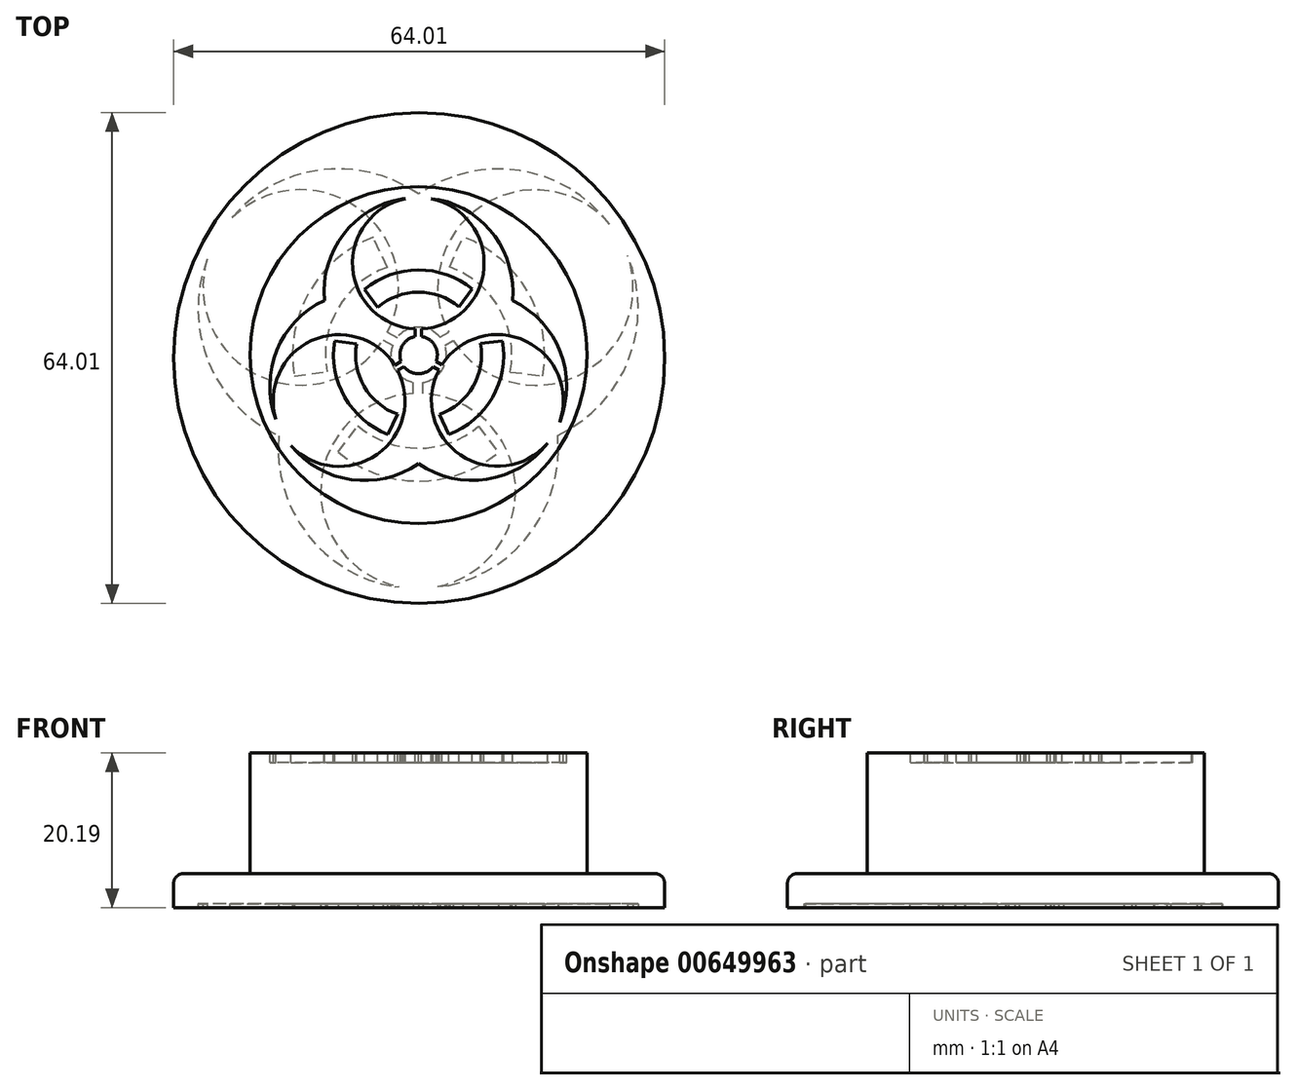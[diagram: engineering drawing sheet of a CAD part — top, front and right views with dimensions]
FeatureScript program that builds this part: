
annotation { "Feature Type Name" : "Feature", "Feature Type Description" : "" }
export const myFeature = defineFeature(function(context is Context, id is Id, definition is map)
    precondition{}
    {
        {
            var Q0;
            Q0=qCreatedBy(makeId("Top.planeOp"),FACE);
            var sketch = newSketch(context, id + "F0", { "sketchPlane" : qUnion([Q0])});
            skCircle(sketch, "E0", {"center": v(0.07, -0.4) * mm, "radius": 32 * mm});
            skSolve(sketch);
        }
        {
            var Q0;
            Q0=makeQuery(id+"F0.imprint","IMPRINT",FACE,{"disambiguationData":[TD([[makeQuery(id+"F0.imprint","IMPRINT",EDGE,{"derivedFrom":sQuery(id+"F0.wireOp",EDGE,"E0")}),1.0]])]});
            extrude(context, id + "F1", {"entities" : qUnion([Q0]), "depth" : 4.44 * mm, "offsetDistance" : 25.4 * mm});
        }
        {
            var Q0;
            Q0=makeQuery(id+"F1.opExtrude","CAP_FACE",FACE,{"disambiguationData":[OSD([sQuery(id+"F0.wireOp",EDGE,"E0")])],"isStart":false});
            var sketch = newSketch(context, id + "F2", { "sketchPlane" : qUnion([Q0])});
            skCircle(sketch, "E1", {"center": v(0, 0) * mm, "radius": 21.97 * mm});
            skSolve(sketch);
        }
        {
            var Q0;
            Q0 = qSketchRegion(id + "F2", true);
            extrude(context, id + "F3", {"entities" : qUnion([Q0]), "operationType" : NewBodyOperationType.ADD, "depth" : 15.75 * mm, "offsetDistance" : 25.4 * mm});
        }
        {
            var Q0;
            Q0=makeQuery(id+"F1.opExtrude","CAP_EDGE",EDGE,{"disambiguationData":[OSD([sQuery(id+"F0.wireOp",EDGE,"E0")])],"isStart":false});
            fillet(context, id + "F4", {"entities" : qUnion([Q0]), "radius" : 1.27 * mm, "tangentPropagation" : true, "allowEdgeOverflow" : false});
        }
        {
            var Q0;
            Q0=makeQuery(id+"F3.opExtrude","CAP_FACE",FACE,{"disambiguationData":[OSD([sQuery(id+"F2.wireOp",EDGE,"E1")])],"isStart":false});
            var sketch = newSketch(context, id + "F5", { "sketchPlane" : qUnion([Q0])});
            skArc(sketch, "E2", {"start": v(-0.47, 2.4) * mm, "mid": v(-2.13, 1.2) * mm, "end": v(-2.29, -0.86) * mm});
            skArc(sketch, "E3", {"start": v(2.64, -1.99) * mm, "mid": v(5.47, -13.06) * mm, "end": v(16.8, -11.51) * mm});
            skPoint(sketch, "E3.first.point", {"position": v(1.98, -8.2) * mm});
            skPoint(sketch, "E3.second.point", {"position": v(5.37, 1.13) * mm});
            skPoint(sketch, "E3.third.point", {"position": v(18.4, -3.15) * mm});
            skArc(sketch, "E4", {"start": v(-3.12, -1.32) * mm, "mid": v(-13.95, 1.86) * mm, "end": v(-18.6, -8.42) * mm});
            skPoint(sketch, "E4.first.point", {"position": v(-17.7, -1.47) * mm});
            skPoint(sketch, "E4.second.point", {"position": v(-6.4, 1.68) * mm});
            skPoint(sketch, "E4.third.point", {"position": v(-5.15, -12.78) * mm});
            skArc(sketch, "E5", {"start": v(0.4, 3.4) * mm, "mid": v(8.5, 11.33) * mm, "end": v(1.65, 20.36) * mm});
            skPoint(sketch, "E5.first.point", {"position": v(-6.26, 17.86) * mm});
            skPoint(sketch, "E5.second.point", {"position": v(-3.87, 4.3) * mm});
            skPoint(sketch, "E5.third.point", {"position": v(8.39, 10.37) * mm});
            skPoint(sketch, "E6.first.point", {"position": v(-12.33, 7.91) * mm});
            skPoint(sketch, "E6.second.point", {"position": v(-4.97, 19.53) * mm});
            skPoint(sketch, "E6.third.point", {"position": v(11.27, 13.16) * mm});
            skArc(sketch, "E7", {"start": v(-12.28, 7.12) * mm, "mid": v(-18.49, 0.6) * mm, "end": v(-18.6, -8.42) * mm});
            skPoint(sketch, "E7.first.point", {"position": v(-12.86, 6.83) * mm});
            skPoint(sketch, "E7.second.point", {"position": v(-19.23, -2.03) * mm});
            skPoint(sketch, "E7.third.point", {"position": v(-1.71, -15.15) * mm});
            skPoint(sketch, "E8.first.point", {"position": v(0.5, -14.49) * mm});
            skPoint(sketch, "E8.second.point", {"position": v(13.68, -14.4) * mm});
            skPoint(sketch, "E8.third.point", {"position": v(14.43, 5.75) * mm});
            skArc(sketch, "E9", {"start": v(-10.94, 1.85) * mm, "mid": v(-9.64, -5.5) * mm, "end": v(-3.98, -10.35) * mm});
            skArc(sketch, "E10", {"start": v(-8.07, 1.46) * mm, "mid": v(-7.1, -4.1) * mm, "end": v(-2.76, -7.72) * mm});
            skLineSegment(sketch, "E11", {"start": v(-7.07, 8.55) * mm, "end": v(-5.34, 6.22) * mm});
            skLineSegment(sketch, "E12", {"start": v(5.28, 6.27) * mm, "end": v(7.01, 8.6) * mm});
            skLineSegment(sketch, "E13", {"start": v(8.06, 1.49) * mm, "end": v(10.94, 1.85) * mm});
            skLineSegment(sketch, "E14", {"start": v(-10.94, 1.85) * mm, "end": v(-8.07, 1.46) * mm});
            skLineSegment(sketch, "E15", {"start": v(-0.47, 3.4) * mm, "end": v(-0.47, 2.4) * mm});
            skLineSegment(sketch, "E16", {"start": v(0.4, 3.4) * mm, "end": v(0.4, 2.41) * mm});
            skLineSegment(sketch, "E17", {"start": v(-3.12, -1.32) * mm, "end": v(-2.29, -0.86) * mm});
            skLineSegment(sketch, "E18", {"start": v(-2.72, -2.01) * mm, "end": v(-1.89, -1.55) * mm});
            skLineSegment(sketch, "E19", {"start": v(1.88, -1.56) * mm, "end": v(2.64, -1.99) * mm});
            skLineSegment(sketch, "E20", {"start": v(2.3, -0.83) * mm, "end": v(3.04, -1.29) * mm});
            skArc(sketch, "E21.trimOffspring", {"start": v(5.28, 6.27) * mm, "mid": v(-0.04, 8.2) * mm, "end": v(-5.34, 6.22) * mm});
            skArc(sketch, "E22.trimOffspring", {"start": v(-0.01, -14.15) * mm, "mid": v(8.92, -16.2) * mm, "end": v(16.8, -11.51) * mm});
            skArc(sketch, "E23.trimOffspring", {"start": v(7.01, 8.6) * mm, "mid": v(-0.04, 11.1) * mm, "end": v(-7.07, 8.55) * mm});
            skArc(sketch, "E24.trimOffspring", {"start": v(-1.89, -1.55) * mm, "mid": v(0, -2.44) * mm, "end": v(1.88, -1.56) * mm});
            skArc(sketch, "E25.trimOffspring", {"start": v(2.3, -0.83) * mm, "mid": v(2.1, 1.24) * mm, "end": v(0.4, 2.41) * mm});
            skArc(sketch, "E26.trimOffspring", {"start": v(12.23, 7.08) * mm, "mid": v(9.95, 15.48) * mm, "end": v(2.68, 20.27) * mm});
            skArc(sketch, "E27.trimOffspring", {"start": v(-16.62, -11.83) * mm, "mid": v(-8.77, -16.25) * mm, "end": v(-0.01, -14.15) * mm});
            skArc(sketch, "E28.trimOffspring", {"start": v(-16.62, -11.83) * mm, "mid": v(-5.4, -12.96) * mm, "end": v(-2.72, -2.01) * mm});
            skLineSegment(sketch, "E29", {"start": v(-2.76, -7.72) * mm, "end": v(-3.98, -10.35) * mm});
            skLineSegment(sketch, "E30", {"start": v(2.72, -7.73) * mm, "end": v(3.91, -10.38) * mm});
            skArc(sketch, "E31.trimOffspring", {"start": v(2.72, -7.73) * mm, "mid": v(7.1, -4.1) * mm, "end": v(8.06, 1.49) * mm});
            skArc(sketch, "E32.trimOffspring", {"start": v(3.91, -10.38) * mm, "mid": v(9.62, -5.53) * mm, "end": v(10.94, 1.85) * mm});
            skArc(sketch, "E33.trimOffspring", {"start": v(18.38, -8.75) * mm, "mid": v(18.47, 0.4) * mm, "end": v(12.23, 7.08) * mm});
            skArc(sketch, "E34.trimOffspring", {"start": v(18.38, -8.75) * mm, "mid": v(14.02, 1.8) * mm, "end": v(3.04, -1.29) * mm});
            skLineSegment(sketch, "E35", {"start": v(-2.1, 20.4) * mm, "end": v(-1.73, 20.36) * mm});
            skLineSegment(sketch, "E36", {"start": v(1.65, 20.36) * mm, "end": v(2.68, 20.27) * mm});
            skArc(sketch, "E37.trimOffspring", {"start": v(-1.73, 20.36) * mm, "mid": v(-8.58, 11.33) * mm, "end": v(-0.47, 3.4) * mm});
            skArc(sketch, "E38.trimOffspring", {"start": v(-2.1, 20.4) * mm, "mid": v(-9.8, 15.75) * mm, "end": v(-12.28, 7.12) * mm});
            skSolve(sketch);
        }
        {
            var Q0;
            Q0=makeQuery(id+"F5.imprint","IMPRINT",FACE,{"disambiguationData":[TD([[makeQuery(id+"F5.imprint","IMPRINT",EDGE,{"derivedFrom":sQuery(id+"F5.wireOp",EDGE,"E2")}),-1.0]])]});
            var Q1;
            Q1=makeQuery(id+"F5.imprint","IMPRINT",FACE,{"disambiguationData":[TD([[makeQuery(id+"F5.imprint","IMPRINT",EDGE,{"derivedFrom":sQuery(id+"F5.wireOp",EDGE,"E11")}),1.0]])]});
            var Q2;
            Q2=makeQuery(id+"F5.imprint","IMPRINT",FACE,{"disambiguationData":[TD([[makeQuery(id+"F5.imprint","IMPRINT",EDGE,{"derivedFrom":sQuery(id+"F5.wireOp",EDGE,"E5")}),-1.0]])]});
            var Q3;
            Q3=makeQuery(id+"F5.imprint","IMPRINT",FACE,{"disambiguationData":[TD([[makeQuery(id+"F5.imprint","IMPRINT",EDGE,{"derivedFrom":sQuery(id+"F5.wireOp",EDGE,"E13")}),-1.0]])]});
            var Q4;
            Q4=makeQuery(id+"F5.imprint","IMPRINT",FACE,{"disambiguationData":[TD([[makeQuery(id+"F5.imprint","IMPRINT",EDGE,{"derivedFrom":sQuery(id+"F5.wireOp",EDGE,"E3")}),-1.0]])]});
            var Q5;
            Q5=makeQuery(id+"F5.imprint","IMPRINT",FACE,{"disambiguationData":[TD([[makeQuery(id+"F5.imprint","IMPRINT",EDGE,{"derivedFrom":sQuery(id+"F5.wireOp",EDGE,"E9")}),1.0]])]});
            extrude(context, id + "F6", {"entities" : qUnion([Q0, Q1, Q2, Q3, Q4, Q5]), "operationType" : NewBodyOperationType.REMOVE, "oppositeDirection" : true, "depth" : 1.27 * mm, "offsetDistance" : 25.4 * mm});
        }
        {
            var Q0;
            Q0=makeQuery(id+"F1.opExtrude","CAP_FACE",FACE,{"disambiguationData":[OSD([sQuery(id+"F0.wireOp",EDGE,"E0")])],"isStart":true});
            var sketch = newSketch(context, id + "F7", { "sketchPlane" : qUnion([Q0])});
            skArc(sketch, "E39", {"start": v(-0.7, 3.56) * mm, "mid": v(-3.16, 1.77) * mm, "end": v(-3.4, -1.27) * mm});
            skArc(sketch, "E40", {"start": v(3.9, -2.95) * mm, "mid": v(8.11, -19.36) * mm, "end": v(24.9, -17.07) * mm});
            skPoint(sketch, "E40.first.point", {"position": v(2.94, -12.16) * mm});
            skPoint(sketch, "E40.second.point", {"position": v(7.97, 1.67) * mm});
            skPoint(sketch, "E40.third.point", {"position": v(27.28, -4.67) * mm});
            skArc(sketch, "E41", {"start": v(-4.63, -1.95) * mm, "mid": v(-20.68, 2.76) * mm, "end": v(-27.57, -12.48) * mm});
            skPoint(sketch, "E41.first.point", {"position": v(-26.24, -2.18) * mm});
            skPoint(sketch, "E41.second.point", {"position": v(-9.5, 2.49) * mm});
            skPoint(sketch, "E41.third.point", {"position": v(-7.64, -18.95) * mm});
            skArc(sketch, "E42", {"start": v(0.59, 5.04) * mm, "mid": v(12.62, 16.8) * mm, "end": v(2.45, 30.2) * mm});
            skPoint(sketch, "E42.first.point", {"position": v(-9.28, 26.47) * mm});
            skPoint(sketch, "E42.second.point", {"position": v(-5.74, 6.37) * mm});
            skPoint(sketch, "E42.third.point", {"position": v(12.43, 15.38) * mm});
            skPoint(sketch, "E43.first.point", {"position": v(-17.85, 10.16) * mm});
            skPoint(sketch, "E43.second.point", {"position": v(-6.95, 27.39) * mm});
            skPoint(sketch, "E43.third.point", {"position": v(17.13, 17.94) * mm});
            skArc(sketch, "E44", {"start": v(-18.2, 10.56) * mm, "mid": v(-27.41, 0.88) * mm, "end": v(-27.57, -12.48) * mm});
            skPoint(sketch, "E44.first.point", {"position": v(-19.06, 10.13) * mm});
            skPoint(sketch, "E44.second.point", {"position": v(-28.5, -3) * mm});
            skPoint(sketch, "E44.third.point", {"position": v(-2.54, -22.46) * mm});
            skPoint(sketch, "E45.first.point", {"position": v(1.16, -23.06) * mm});
            skPoint(sketch, "E45.second.point", {"position": v(20.7, -22.92) * mm});
            skPoint(sketch, "E45.third.point", {"position": v(21.82, 6.95) * mm});
            skArc(sketch, "E46", {"start": v(-16.22, 2.75) * mm, "mid": v(-14.3, -8.14) * mm, "end": v(-5.9, -15.35) * mm});
            skArc(sketch, "E47", {"start": v(-11.96, 2.17) * mm, "mid": v(-10.52, -6.08) * mm, "end": v(-4.1, -11.45) * mm});
            skLineSegment(sketch, "E48", {"start": v(-10.48, 12.68) * mm, "end": v(-7.91, 9.22) * mm});
            skLineSegment(sketch, "E49", {"start": v(7.83, 9.3) * mm, "end": v(10.4, 12.75) * mm});
            skLineSegment(sketch, "E50", {"start": v(11.95, 2.2) * mm, "end": v(16.22, 2.74) * mm});
            skLineSegment(sketch, "E51", {"start": v(-16.22, 2.75) * mm, "end": v(-11.96, 2.17) * mm});
            skLineSegment(sketch, "E52", {"start": v(-0.7, 5.04) * mm, "end": v(-0.7, 3.56) * mm});
            skLineSegment(sketch, "E53", {"start": v(0.59, 5.04) * mm, "end": v(0.59, 3.58) * mm});
            skLineSegment(sketch, "E54", {"start": v(-4.63, -1.95) * mm, "end": v(-3.4, -1.27) * mm});
            skLineSegment(sketch, "E55", {"start": v(-4.04, -2.98) * mm, "end": v(-2.8, -2.3) * mm});
            skLineSegment(sketch, "E56", {"start": v(2.8, -2.31) * mm, "end": v(3.9, -2.95) * mm});
            skLineSegment(sketch, "E57", {"start": v(3.4, -1.23) * mm, "end": v(4.5, -1.9) * mm});
            skArc(sketch, "E58.trimOffspring", {"start": v(7.83, 9.3) * mm, "mid": v(-0.05, 12.15) * mm, "end": v(-7.91, 9.22) * mm});
            skArc(sketch, "E59.trimOffspring", {"start": v(-0.02, -20.99) * mm, "mid": v(13.22, -24.04) * mm, "end": v(24.9, -17.07) * mm});
            skArc(sketch, "E60.trimOffspring", {"start": v(10.4, 12.75) * mm, "mid": v(-0.05, 16.45) * mm, "end": v(-10.48, 12.68) * mm});
            skArc(sketch, "E61.trimOffspring", {"start": v(-2.8, -2.3) * mm, "mid": v(0, -3.62) * mm, "end": v(2.8, -2.31) * mm});
            skArc(sketch, "E62.trimOffspring", {"start": v(3.4, -1.23) * mm, "mid": v(3.13, 1.84) * mm, "end": v(0.59, 3.58) * mm});
            skArc(sketch, "E63.trimOffspring", {"start": v(18.13, 10.5) * mm, "mid": v(14.75, 22.95) * mm, "end": v(3.97, 30.06) * mm});
            skArc(sketch, "E64.trimOffspring", {"start": v(-24.64, -17.55) * mm, "mid": v(-13, -24.1) * mm, "end": v(-0.02, -20.99) * mm});
            skArc(sketch, "E65.trimOffspring", {"start": v(-24.64, -17.55) * mm, "mid": v(-8.01, -19.22) * mm, "end": v(-4.04, -2.98) * mm});
            skLineSegment(sketch, "E66", {"start": v(-4.1, -11.45) * mm, "end": v(-5.9, -15.35) * mm});
            skLineSegment(sketch, "E67", {"start": v(4.04, -11.46) * mm, "end": v(5.8, -15.4) * mm});
            skArc(sketch, "E68.trimOffspring", {"start": v(4.04, -11.46) * mm, "mid": v(10.52, -6.1) * mm, "end": v(11.95, 2.2) * mm});
            skArc(sketch, "E69.trimOffspring", {"start": v(5.8, -15.4) * mm, "mid": v(14.26, -8.2) * mm, "end": v(16.22, 2.74) * mm});
            skArc(sketch, "E70.trimOffspring", {"start": v(27.26, -12.97) * mm, "mid": v(27.4, 0.59) * mm, "end": v(18.13, 10.5) * mm});
            skArc(sketch, "E71.trimOffspring", {"start": v(27.26, -12.97) * mm, "mid": v(20.8, 2.66) * mm, "end": v(4.5, -1.9) * mm});
            skLineSegment(sketch, "E72", {"start": v(-3.1, 30.24) * mm, "end": v(-2.56, 30.2) * mm});
            skLineSegment(sketch, "E73", {"start": v(2.45, 30.2) * mm, "end": v(3.97, 30.06) * mm});
            skArc(sketch, "E74.trimOffspring", {"start": v(-2.56, 30.2) * mm, "mid": v(-12.73, 16.8) * mm, "end": v(-0.7, 5.04) * mm});
            skArc(sketch, "E75.trimOffspring", {"start": v(-3.1, 30.24) * mm, "mid": v(-14.52, 23.36) * mm, "end": v(-18.2, 10.56) * mm});
            skSolve(sketch);
        }
        {
            var Q0;
            Q0=makeQuery(id+"F7.imprint","IMPRINT",FACE,{"disambiguationData":[TD([[makeQuery(id+"F7.imprint","IMPRINT",EDGE,{"derivedFrom":sQuery(id+"F7.wireOp",EDGE,"E39")}),-1.0]])]});
            var Q1;
            Q1=makeQuery(id+"F7.imprint","IMPRINT",FACE,{"disambiguationData":[TD([[makeQuery(id+"F7.imprint","IMPRINT",EDGE,{"derivedFrom":sQuery(id+"F7.wireOp",EDGE,"E48")}),1.0]])]});
            var Q2;
            Q2=makeQuery(id+"F7.imprint","IMPRINT",FACE,{"disambiguationData":[TD([[makeQuery(id+"F7.imprint","IMPRINT",EDGE,{"derivedFrom":sQuery(id+"F7.wireOp",EDGE,"E42")}),-1.0]])]});
            var Q3;
            Q3=makeQuery(id+"F7.imprint","IMPRINT",FACE,{"disambiguationData":[TD([[makeQuery(id+"F7.imprint","IMPRINT",EDGE,{"derivedFrom":sQuery(id+"F7.wireOp",EDGE,"E50")}),-1.0]])]});
            var Q4;
            Q4=makeQuery(id+"F7.imprint","IMPRINT",FACE,{"disambiguationData":[TD([[makeQuery(id+"F7.imprint","IMPRINT",EDGE,{"derivedFrom":sQuery(id+"F7.wireOp",EDGE,"E40")}),-1.0]])]});
            var Q5;
            Q5=makeQuery(id+"F7.imprint","IMPRINT",FACE,{"disambiguationData":[TD([[makeQuery(id+"F7.imprint","IMPRINT",EDGE,{"derivedFrom":sQuery(id+"F7.wireOp",EDGE,"E46")}),1.0]])]});
            extrude(context, id + "F8", {"entities" : qUnion([Q0, Q1, Q2, Q3, Q4, Q5]), "operationType" : NewBodyOperationType.REMOVE, "oppositeDirection" : true, "depth" : 0.5 * mm, "offsetDistance" : 25.4 * mm});
        }
    });
